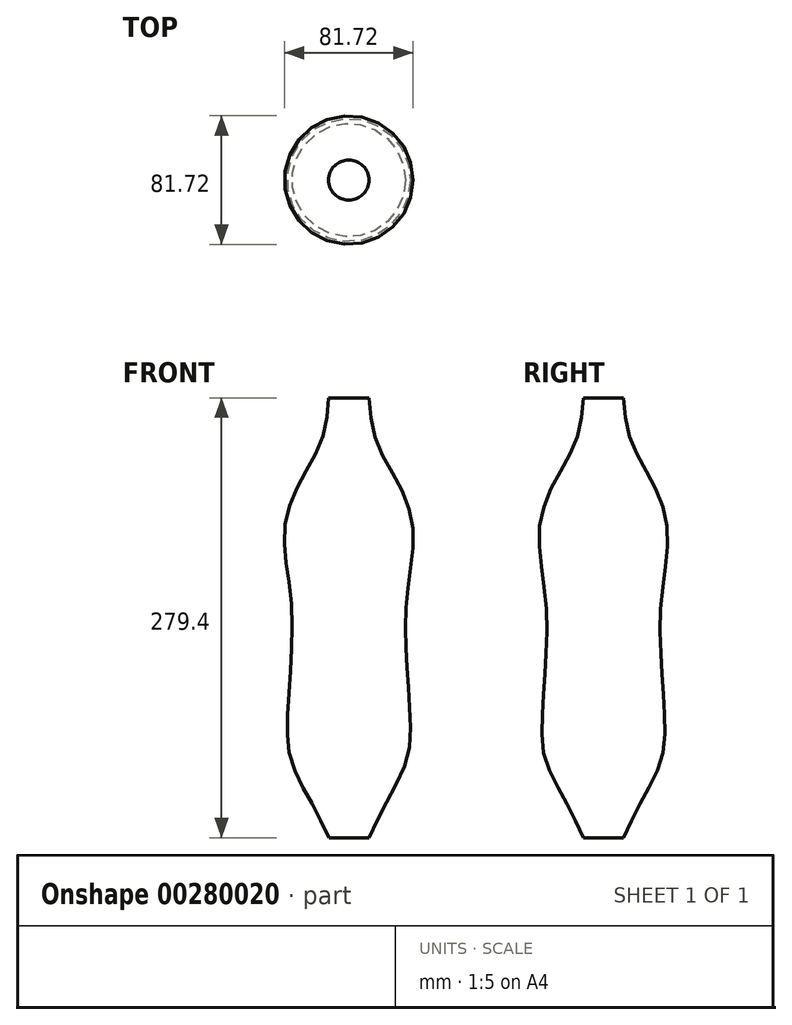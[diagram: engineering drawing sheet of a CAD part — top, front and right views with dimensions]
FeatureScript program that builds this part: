
annotation { "Feature Type Name" : "Feature", "Feature Type Description" : "" }
export const myFeature = defineFeature(function(context is Context, id is Id, definition is map)
    precondition{}
    {
        {
            var Q0;
            Q0=qCreatedBy(makeId("Top.planeOp"),FACE);
            cPlane(context, id + "F0", {"entities" : qUnion([Q0]), "cplaneType" : CPlaneType.OFFSET, "offset" : 25.4 * mm, "width" : 152.4 * mm, "height" : 152.4 * mm});
        }
        {
            var Q0;
            Q0=qCreatedBy(id+"F0.planeOp",FACE);
            cPlane(context, id + "F1", {"entities" : qUnion([Q0]), "cplaneType" : CPlaneType.OFFSET, "offset" : 25.4 * mm, "width" : 152.4 * mm, "height" : 152.4 * mm});
        }
        {
            var Q0;
            Q0=qCreatedBy(id+"F1.planeOp",FACE);
            cPlane(context, id + "F2", {"entities" : qUnion([Q0]), "cplaneType" : CPlaneType.OFFSET, "offset" : 25.4 * mm, "width" : 152.4 * mm, "height" : 152.4 * mm});
        }
        {
            var Q0;
            Q0=qCreatedBy(id+"F2.planeOp",FACE);
            cPlane(context, id + "F3", {"entities" : qUnion([Q0]), "cplaneType" : CPlaneType.OFFSET, "offset" : 76.2 * mm, "width" : 152.4 * mm, "height" : 152.4 * mm});
        }
        {
            var Q0;
            Q0=qCreatedBy(id+"F3.planeOp",FACE);
            cPlane(context, id + "F4", {"entities" : qUnion([Q0]), "cplaneType" : CPlaneType.OFFSET, "offset" : 50.8 * mm, "width" : 152.4 * mm, "height" : 152.4 * mm});
        }
        {
            var Q0;
            Q0=qCreatedBy(id+"F4.planeOp",FACE);
            cPlane(context, id + "F5", {"entities" : qUnion([Q0]), "cplaneType" : CPlaneType.OFFSET, "offset" : 25.4 * mm, "width" : 152.4 * mm, "height" : 152.4 * mm});
        }
        {
            var Q0;
            Q0=qCreatedBy(id+"F5.planeOp",FACE);
            cPlane(context, id + "F6", {"entities" : qUnion([Q0]), "cplaneType" : CPlaneType.OFFSET, "offset" : 25.4 * mm, "width" : 152.4 * mm, "height" : 152.4 * mm});
        }
        {
            var Q0;
            Q0=qCreatedBy(makeId("Top.planeOp"),FACE);
            var sketch = newSketch(context, id + "F7", { "sketchPlane" : qUnion([Q0])});
            skCircle(sketch, "E0", {"center": v(0, 0) * mm, "radius": 12.7 * mm});
            skSolve(sketch);
        }
        {
            var Q0;
            Q0=qCreatedBy(id+"F0.planeOp",FACE);
            var sketch = newSketch(context, id + "F8", { "sketchPlane" : qUnion([Q0])});
            skCircle(sketch, "E1", {"center": v(0, 0) * mm, "radius": 25.4 * mm});
            skSolve(sketch);
        }
        {
            var Q0;
            Q0=qCreatedBy(id+"F1.planeOp",FACE);
            var sketch = newSketch(context, id + "F9", { "sketchPlane" : qUnion([Q0])});
            skCircle(sketch, "E2", {"center": v(0, 0) * mm, "radius": 37.2 * mm});
            skSolve(sketch);
        }
        {
            var Q0;
            Q0=qCreatedBy(id+"F2.planeOp",FACE);
            var sketch = newSketch(context, id + "F10", { "sketchPlane" : qUnion([Q0])});
            skCircle(sketch, "E3", {"center": v(0, 0) * mm, "radius": 38.91 * mm});
            skSolve(sketch);
        }
        {
            var Q0;
            Q0=qCreatedBy(id+"F3.planeOp",FACE);
            var sketch = newSketch(context, id + "F11", { "sketchPlane" : qUnion([Q0])});
            skCircle(sketch, "E4", {"center": v(0, 0) * mm, "radius": 36.86 * mm});
            skSolve(sketch);
        }
        {
            var Q0;
            Q0=qCreatedBy(id+"F4.planeOp",FACE);
            var sketch = newSketch(context, id + "F12", { "sketchPlane" : qUnion([Q0])});
            skCircle(sketch, "E5", {"center": v(0, 0) * mm, "radius": 39.72 * mm});
            skSolve(sketch);
        }
        {
            var Q0;
            Q0=qCreatedBy(id+"F5.planeOp",FACE);
            var sketch = newSketch(context, id + "F13", { "sketchPlane" : qUnion([Q0])});
            skCircle(sketch, "E6", {"center": v(0, 0) * mm, "radius": 29.6 * mm});
            skSolve(sketch);
        }
        {
            var Q0;
            Q0=qCreatedBy(id+"F6.planeOp",FACE);
            var sketch = newSketch(context, id + "F14", { "sketchPlane" : qUnion([Q0])});
            skCircle(sketch, "E7", {"center": v(0, 0) * mm, "radius": 16.72 * mm});
            skSolve(sketch);
        }
        {
            var Q0;
            Q0=qCreatedBy(id+"F6.planeOp",FACE);
            cPlane(context, id + "F15", {"entities" : qUnion([Q0]), "cplaneType" : CPlaneType.OFFSET, "offset" : 25.4 * mm, "width" : 152.4 * mm, "height" : 152.4 * mm});
        }
        {
            var Q0;
            Q0=qCreatedBy(id+"F15.planeOp",FACE);
            var sketch = newSketch(context, id + "F16", { "sketchPlane" : qUnion([Q0])});
            skCircle(sketch, "E8", {"center": v(0, 0) * mm, "radius": 12.78 * mm});
            skSolve(sketch);
        }
        {
            var Q0;
            Q0=makeQuery(id+"F7.imprint","IMPRINT",FACE,{"disambiguationData":[TD([[makeQuery(id+"F7.imprint","IMPRINT",EDGE,{"derivedFrom":sQuery(id+"F7.wireOp",EDGE,"E0")}),1.0]])]});
            var Q1;
            Q1=makeQuery(id+"F8.imprint","IMPRINT",FACE,{"disambiguationData":[TD([[makeQuery(id+"F8.imprint","IMPRINT",EDGE,{"derivedFrom":sQuery(id+"F8.wireOp",EDGE,"E1")}),1.0]])]});
            var Q2;
            Q2=makeQuery(id+"F9.imprint","IMPRINT",FACE,{"disambiguationData":[TD([[makeQuery(id+"F9.imprint","IMPRINT",EDGE,{"derivedFrom":sQuery(id+"F9.wireOp",EDGE,"E2")}),1.0]])]});
            var Q3;
            Q3=makeQuery(id+"F10.imprint","IMPRINT",FACE,{"disambiguationData":[TD([[makeQuery(id+"F10.imprint","IMPRINT",EDGE,{"derivedFrom":sQuery(id+"F10.wireOp",EDGE,"E3")}),1.0]])]});
            var Q4;
            Q4=makeQuery(id+"F11.imprint","IMPRINT",FACE,{"disambiguationData":[TD([[makeQuery(id+"F11.imprint","IMPRINT",EDGE,{"derivedFrom":sQuery(id+"F11.wireOp",EDGE,"E4")}),1.0]])]});
            var Q5;
            Q5=makeQuery(id+"F12.imprint","IMPRINT",FACE,{"disambiguationData":[TD([[makeQuery(id+"F12.imprint","IMPRINT",EDGE,{"derivedFrom":sQuery(id+"F12.wireOp",EDGE,"E5")}),1.0]])]});
            var Q6;
            Q6=makeQuery(id+"F13.imprint","IMPRINT",FACE,{"disambiguationData":[TD([[makeQuery(id+"F13.imprint","IMPRINT",EDGE,{"derivedFrom":sQuery(id+"F13.wireOp",EDGE,"E6")}),1.0]])]});
            var Q7;
            Q7=makeQuery(id+"F14.imprint","IMPRINT",FACE,{"disambiguationData":[TD([[makeQuery(id+"F14.imprint","IMPRINT",EDGE,{"derivedFrom":sQuery(id+"F14.wireOp",EDGE,"E7")}),1.0]])]});
            var Q8;
            Q8=makeQuery(id+"F16.imprint","IMPRINT",FACE,{"disambiguationData":[TD([[makeQuery(id+"F16.imprint","IMPRINT",EDGE,{"derivedFrom":sQuery(id+"F16.wireOp",EDGE,"E8")}),1.0]])]});
            loft(context, id + "F17", {"sheetProfilesArray" : [{ "sheetProfileEntities" : qUnion([Q0]) }, { "sheetProfileEntities" : qUnion([Q1]) }, { "sheetProfileEntities" : qUnion([Q2]) }, { "sheetProfileEntities" : qUnion([Q3]) }, { "sheetProfileEntities" : qUnion([Q4]) }, { "sheetProfileEntities" : qUnion([Q5]) }, { "sheetProfileEntities" : qUnion([Q6]) }, { "sheetProfileEntities" : qUnion([Q7]) }, { "sheetProfileEntities" : qUnion([Q8]) }]});
        }
    });
